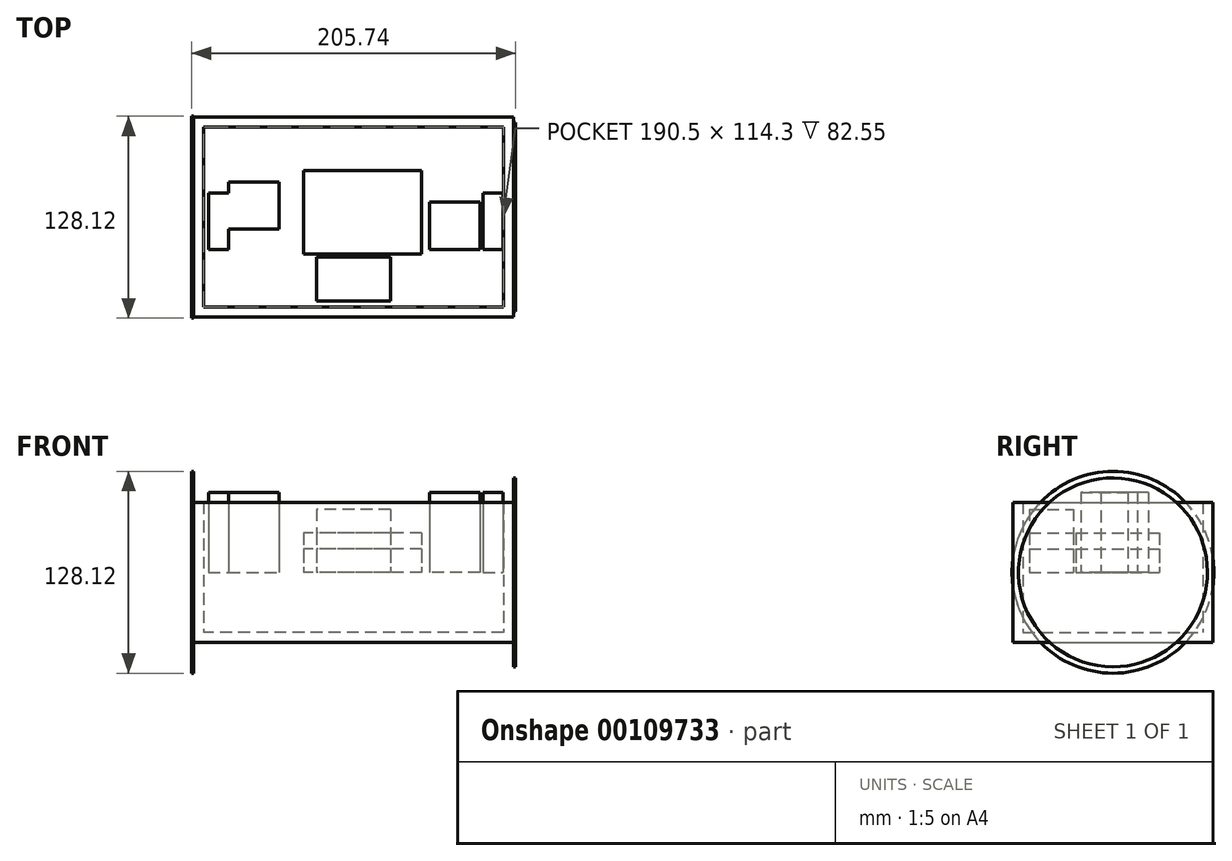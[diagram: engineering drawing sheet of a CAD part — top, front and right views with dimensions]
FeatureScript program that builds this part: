
annotation { "Feature Type Name" : "Feature", "Feature Type Description" : "" }
export const myFeature = defineFeature(function(context is Context, id is Id, definition is map)
    precondition{}
    {
        {
            var Q0;
            Q0=qCreatedBy(makeId("Top.planeOp"),FACE);
            var sketch = newSketch(context, id + "F0", { "sketchPlane" : qUnion([Q0])});
            skLineSegment(sketch, "E0.bottom", {"start": v(101.6, -63.5) * mm, "end": v(-101.6, -63.5) * mm});
            skLineSegment(sketch, "E0.top", {"start": v(101.6, 63.5) * mm, "end": v(-101.6, 63.5) * mm});
            skLineSegment(sketch, "E0.left", {"start": v(101.6, -63.5) * mm, "end": v(101.6, 63.5) * mm});
            skLineSegment(sketch, "E0.right", {"start": v(-101.6, -63.5) * mm, "end": v(-101.6, 63.5) * mm});
            skPoint(sketch, "E0.middle", {"position": v(0, 0) * mm});
            skLineSegment(sketch, "E1.bottom", {"start": v(202.9, -126.67) * mm, "end": v(0.3, -126.67) * mm});
            skLineSegment(sketch, "E1.left", {"start": v(202.9, -126.67) * mm, "end": v(202.9, -0.33) * mm});
            skPoint(sketch, "E1.middle", {"position": v(101.6, -63.5) * mm});
            skPoint(sketch, "E2.orphan", {"position": v(0.3, -0.33) * mm});
            skSolve(sketch);
        }
        {
            var Q0;
            Q0=makeQuery(id+"F0.imprint","IMPRINT",FACE,{"disambiguationData":[TD([[makeQuery(id+"F0.imprint","IMPRINT",EDGE,{"derivedFrom":sQuery(id+"F0.wireOp",EDGE,"E0.bottom")}),-1.0]])]});
            extrude(context, id + "F1", {"entities" : qUnion([Q0]), "endBound" : BoundingType.SYMMETRIC, "depth" : 88.9 * mm});
        }
        {
            var Q0;
            Q0=makeQuery(id+"F1.opExtrude","CAP_FACE",FACE,{"disambiguationData":[OSD([sQuery(id+"F0.wireOp",EDGE,"E0.bottom"),sQuery(id+"F0.wireOp",EDGE,"E0.top"),sQuery(id+"F0.wireOp",EDGE,"E0.left"),sQuery(id+"F0.wireOp",EDGE,"E0.right")])],"isStart":false});
            shell(context, id + "F2", {"entities" : qUnion([Q0]), "thickness" : 6.35 * mm});
        }
        {
            var Q0;
            Q0=qCreatedBy(makeId("Top.planeOp"),FACE);
            var sketch = newSketch(context, id + "F3", { "sketchPlane" : qUnion([Q0])});
            skPoint(sketch, "E3.middle", {"position": v(0, 0) * mm});
            skPoint(sketch, "E4.middle", {"position": v(28.67, 24.88) * mm});
            skPoint(sketch, "E5.orphan", {"position": v(-28.67, 23.87) * mm});
            skPoint(sketch, "E4.right.end.orphan", {"position": v(0, 48.88) * mm});
            skPoint(sketch, "E4.bottom.end.orphan", {"position": v(5.75, 2.96) * mm});
            skPoint(sketch, "E3.top.end.orphan", {"position": v(-28.67, -24.88) * mm});
            skPoint(sketch, "E3.top.start.orphan", {"position": v(28.67, -23.87) * mm});
            skPoint(sketch, "E4.left.end.orphan", {"position": v(51.59, 46.8) * mm});
            skPoint(sketch, "E4.left.start.orphan", {"position": v(57.34, 0.88) * mm});
            skLineSegment(sketch, "E6.bottom", {"start": v(43.25, -23.54) * mm, "end": v(-31.75, -23.54) * mm});
            skLineSegment(sketch, "E6.top", {"start": v(43.25, 29.46) * mm, "end": v(-31.75, 29.46) * mm});
            skLineSegment(sketch, "E6.left", {"start": v(43.25, -23.54) * mm, "end": v(43.25, 29.46) * mm});
            skLineSegment(sketch, "E6.right", {"start": v(-31.75, -23.54) * mm, "end": v(-31.75, 29.46) * mm});
            skLineSegment(sketch, "E7.bottom", {"start": v(23.5, -53.2) * mm, "end": v(-23.5, -53.2) * mm});
            skLineSegment(sketch, "E7.top", {"start": v(23.5, -25.18) * mm, "end": v(-23.5, -25.18) * mm});
            skLineSegment(sketch, "E7.left", {"start": v(23.5, -53.2) * mm, "end": v(23.5, -25.18) * mm});
            skLineSegment(sketch, "E7.right", {"start": v(-23.5, -53.2) * mm, "end": v(-23.5, -25.18) * mm});
            skPoint(sketch, "E7.middle", {"position": v(0, -39.19) * mm});
            skSolve(sketch);
        }
        {
            var Q0;
            Q0 = qSketchRegion(id + "F3", true);
            extrude(context, id + "F4", {"entities" : qUnion([Q0]), "operationType" : NewBodyOperationType.ADD, "depth" : 25 * mm});
        }
        {
            var Q0;
            Q0=makeQuery(id+"F1.opExtrude","SWEPT_FACE",FACE,{"disambiguationData":[OSD([sQuery(id+"F0.wireOp",EDGE,"E0.left")])]});
            cPlane(context, id + "F5", {"entities" : qUnion([Q0]), "cplaneType" : CPlaneType.OFFSET, "offset" : 0 * mm, "width" : 152.4 * mm, "height" : 152.4 * mm});
        }
        {
            var Q0;
            Q0=qCreatedBy(id+"F5.planeOp",FACE);
            var sketch = newSketch(context, id + "F6", { "sketchPlane" : qUnion([Q0])});
            skCircle(sketch, "E8", {"center": v(0, 0) * mm, "radius": 60 * mm});
            skSolve(sketch);
        }
        {
            var Q0;
            Q0=makeQuery(id+"F6.imprint","IMPRINT",FACE,{"disambiguationData":[TD([[makeQuery(id+"F6.imprint","IMPRINT",EDGE,{"derivedFrom":sQuery(id+"F6.wireOp",EDGE,"E8")}),1.0]])]});
            extrude(context, id + "F7", {"entities" : qUnion([Q0]), "operationType" : NewBodyOperationType.ADD, "depth" : 1.27 * mm});
        }
        {
            var Q0;
            Q0=makeQuery(id+"F1.opExtrude","SWEPT_FACE",FACE,{"disambiguationData":[OSD([sQuery(id+"F0.wireOp",EDGE,"E0.right")])]});
            cPlane(context, id + "F8", {"entities" : qUnion([Q0]), "cplaneType" : CPlaneType.OFFSET, "offset" : 0 * mm, "width" : 152.4 * mm, "height" : 152.4 * mm});
        }
        {
            var Q0;
            Q0=qCreatedBy(id+"F8.planeOp",FACE);
            var sketch = newSketch(context, id + "F9", { "sketchPlane" : qUnion([Q0])});
            skCircle(sketch, "E9", {"center": v(0, 0) * mm, "radius": 64.06 * mm});
            skSolve(sketch);
        }
        {
            var Q0;
            Q0=makeQuery(id+"F9.imprint","IMPRINT",FACE,{"disambiguationData":[TD([[makeQuery(id+"F9.imprint","IMPRINT",EDGE,{"derivedFrom":sQuery(id+"F9.wireOp",EDGE,"E9")}),1.0]])]});
            extrude(context, id + "F10", {"entities" : qUnion([Q0]), "operationType" : NewBodyOperationType.ADD, "depth" : 1.27 * mm});
        }
        {
            var Q0;
            Q0 = qSketchRegion(id + "F3", true);
            var Q1;
            Q1=makeQuery(id+"F4.opExtrude","CAP_FACE",FACE,{"disambiguationData":[OSD([sQuery(id+"F3.wireOp",EDGE,"E7.bottom"),sQuery(id+"F3.wireOp",EDGE,"E7.top"),sQuery(id+"F3.wireOp",EDGE,"E7.left"),sQuery(id+"F3.wireOp",EDGE,"E7.right")])],"isStart":false});
            extrude(context, id + "F11", {"entities" : qUnion([Q0, Q1]), "depth" : 15 * mm});
        }
        {
            var Q0;
            Q0=qCreatedBy(makeId("Top.planeOp"),FACE);
            var sketch = newSketch(context, id + "F12", { "sketchPlane" : qUnion([Q0])});
            skLineSegment(sketch, "E10.bottom", {"start": v(-92.17, 15.37) * mm, "end": v(-79.47, 15.37) * mm});
            skLineSegment(sketch, "E10.top", {"start": v(-92.17, -20.44) * mm, "end": v(-79.47, -20.44) * mm});
            skLineSegment(sketch, "E10.left", {"start": v(-92.17, 15.37) * mm, "end": v(-92.17, -20.44) * mm});
            skLineSegment(sketch, "E10.right", {"start": v(-79.47, 15.37) * mm, "end": v(-79.47, -20.44) * mm});
            skLineSegment(sketch, "E11.bottom", {"start": v(-79.47, 22.4) * mm, "end": v(-47.47, 22.4) * mm});
            skLineSegment(sketch, "E11.top", {"start": v(-79.47, -7.6) * mm, "end": v(-47.47, -7.6) * mm});
            skLineSegment(sketch, "E11.left", {"start": v(-79.47, 22.4) * mm, "end": v(-79.47, -7.6) * mm});
            skLineSegment(sketch, "E11.right", {"start": v(-47.47, 22.4) * mm, "end": v(-47.47, -7.6) * mm});
            skLineSegment(sketch, "E12.bottom", {"start": v(82.24, 15.37) * mm, "end": v(94.94, 15.37) * mm});
            skLineSegment(sketch, "E12.top", {"start": v(82.24, -20.44) * mm, "end": v(94.94, -20.44) * mm});
            skLineSegment(sketch, "E12.left", {"start": v(82.24, 15.37) * mm, "end": v(82.24, -20.44) * mm});
            skLineSegment(sketch, "E12.right", {"start": v(94.94, 15.37) * mm, "end": v(94.94, -20.44) * mm});
            skLineSegment(sketch, "E13.bottom", {"start": v(80.31, -20.44) * mm, "end": v(48.3, -20.44) * mm});
            skLineSegment(sketch, "E13.top", {"start": v(80.31, 9.56) * mm, "end": v(48.3, 9.56) * mm});
            skLineSegment(sketch, "E13.left", {"start": v(80.31, -20.44) * mm, "end": v(80.31, 9.56) * mm});
            skLineSegment(sketch, "E13.right", {"start": v(48.3, -20.44) * mm, "end": v(48.3, 9.56) * mm});
            skSolve(sketch);
        }
        {
            var Q0;
            Q0 = qSketchRegion(id + "F12", true);
            extrude(context, id + "F13", {"entities" : qUnion([Q0]), "depth" : 50.8 * mm});
        }
    });
